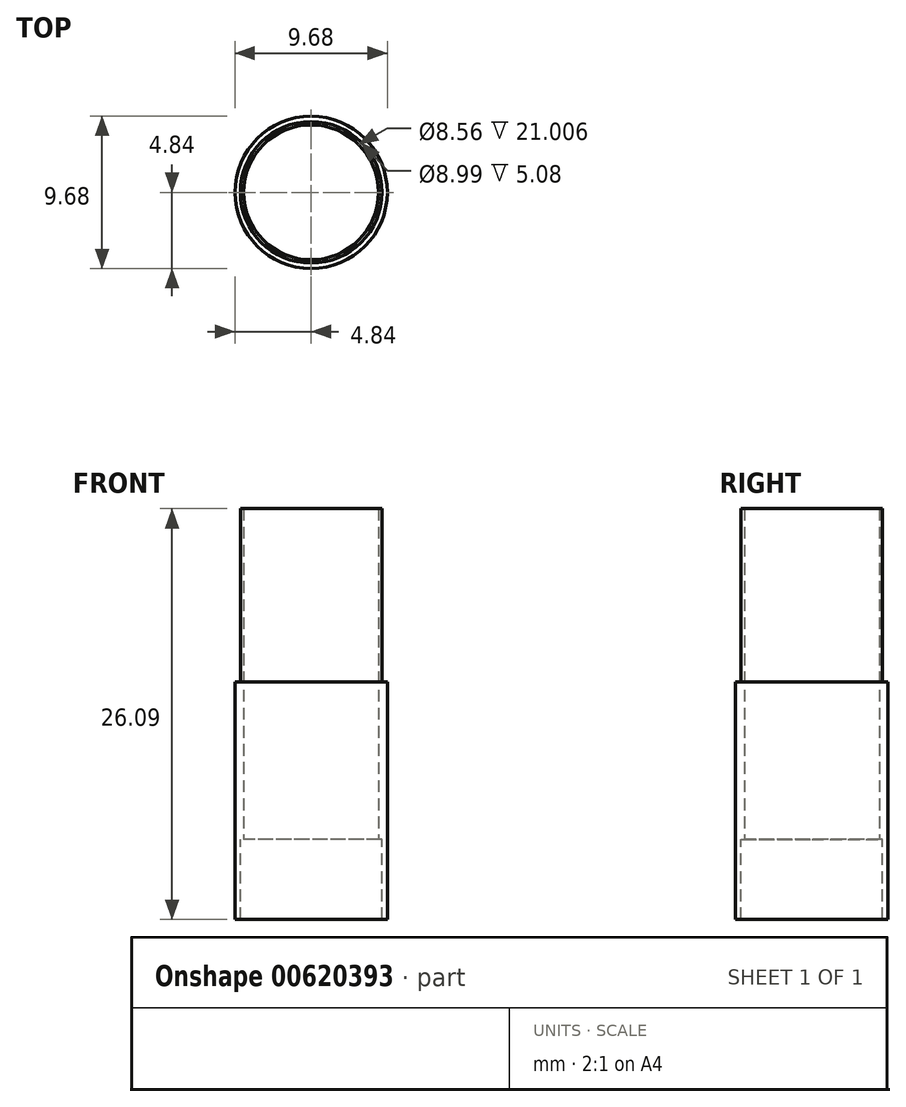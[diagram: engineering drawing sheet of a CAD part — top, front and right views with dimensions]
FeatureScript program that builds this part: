
annotation { "Feature Type Name" : "Feature", "Feature Type Description" : "" }
export const myFeature = defineFeature(function(context is Context, id is Id, definition is map)
    precondition{}
    {
        {
            var Q0;
            Q0=qCreatedBy(makeId("Top.planeOp"),FACE);
            var sketch = newSketch(context, id + "F0", { "sketchPlane" : qUnion([Q0])});
            skCircle(sketch, "E0", {"center": v(0, 0) * mm, "radius": 4.5 * mm});
            skCircle(sketch, "E1", {"center": v(0, 0) * mm, "radius": 4.28 * mm});
            skSolve(sketch);
        }
        {
            var Q0;
            Q0=qSketchRegion(id+"F0",true);
            extrude(context, id + "F1", {"entities" : qUnion([Q0]), "depth" : 21 * mm});
        }
        {
            var Q0;
            Q0=qCreatedBy(makeId("Top.planeOp"),FACE);
            var sketch = newSketch(context, id + "F2", { "sketchPlane" : qUnion([Q0])});
            skCircle(sketch, "E2", {"center": v(0, 0) * mm, "radius": 4.5 * mm});
            skCircle(sketch, "E3", {"center": v(0, 0) * mm, "radius": 4.84 * mm});
            skSolve(sketch);
        }
        {
            var Q0;
            Q0=qSketchRegion(id+"F2",true);
            extrude(context, id + "F3", {"entities" : qUnion([Q0]), "operationType" : NewBodyOperationType.ADD, "depth" : 10 * mm});
        }
        {
            var Q0;
            Q0=makeQuery(id+"F2.imprint","IMPRINT",FACE,{"disambiguationData":[TD([[makeQuery(id+"F2.imprint","IMPRINT",EDGE,{"derivedFrom":sQuery(id+"F2.wireOp",EDGE,"E2")}),-1.0]])]});
            extrude(context, id + "F4", {"entities" : qUnion([Q0]), "operationType" : NewBodyOperationType.ADD, "oppositeDirection" : true, "depth" : 5.08 * mm});
        }
    });
